# Revit family: MAD-442-I_Módulo analógico 2 salidas de tensión
name_source: partatom
category: Dispositivos de alarma de incendios
revit_build: Autodesk Revit 2017 (Build: 20190508_0315(x64)
units: mm (PartAtom-declared; Revit-internal decimal feet)

## family parameters
Anfitrión = Cara
Compartido = No
Corte con vacíos al cargar = No
Cota de conector redondo = Diámetro de uso
Mantener orientación de anotación = No
Punto de cálculo de habitación = No
Tipo de pieza = Normal

## types (1)
- MAD-442-I
    Alimentación auxiliar - Consumo en reposo = < 5 mA
    Alimentación auxiliar - Consumo máx. en alarma = < 100 mA
    Alimentación auxiliar - Tensión de trabajo = 24VDC
    Altura = 100 mm
    Anchura = 100 mm
    Carga eléctrica = Otro
    Certificación = EN 54-18 y EN 54-17
    Comentarios de tipo = Los módulos permiten conectar detectores convencionales al sistema analógico. Son idóneos para aquellas instalaciones que, por el tamaño de área a proteger, necesitan un gran número de elementos de detección puntual, pero todos tienen que dar una misma identificación, por ejemplo, en aparcamientos, pasillos o áreas diáfanas. Instalando estos módulos se pueden reducir costes, ya que permiten añadir detectores convencionales al sistema analógico.
    Conexionado = 2 x 1,5 mm² trenzado y apantallado
    Cuerpo = ABS Rojo
    Código de montaje = PDETMAD-442-I
    Descripción = Módulo monitor analógico con aislador incorporado de 2 zonas convencionales, permite la conexión de hasta 20 detectores convencionales y/o 32 pulsadores convencionales por zona. Marca Detnov, modelo MAD-442-I. Discrimina entre alarma de detector y pulsador. Discrimina la avería por corte o por cortocircuito de la zona. Ocupa dos direcciones de lazo. Precisa alimentación auxiliar de 24 Vcc. Incluye leds indicadores de estado. Conexionado mediante regletas extraíbles de hasta 2,5mm2 de sección. Posibilidad de ser instalado en carril DIN o montaje plano a pared en caja BOX-400. Consumo menor de 300μA en reposo. Color rojo. Dimensiones 100 x 82 x 23 mm. Certificado CPR EN54-18 y EN54-17.
    Elevación por defecto = 1219 mm
    Fabricante = Detnov Security
    Fases = 1
    Humedad relativa = 95% sin condensación
    Imagen de tipo = <Ninguno>
    Lazo - Consumo en alarma = < 3 mA
    Lazo - Consumo en reposo = < 300 μA
    Lazo - Tensión de trabajo = De 22 a 38VDC
    Modelo = Módulo analógico MAD-442-I
    Potencia total = 0 VA
    Profundidad = 23 mm
    Salida - Consumo en reposo = < 5 mA
    Salida - Consumo máx. en alarma = < 100 mA
    Salida - Tensión de trabajo = 24VDC
    Teléfono = (+34) 93 371 60 25
    Temperatura trabajo = De -10ºC a 70ºC
    URL = https://www.detnov.com
    Voltaje = 230 V
    Índice IP = IP40
